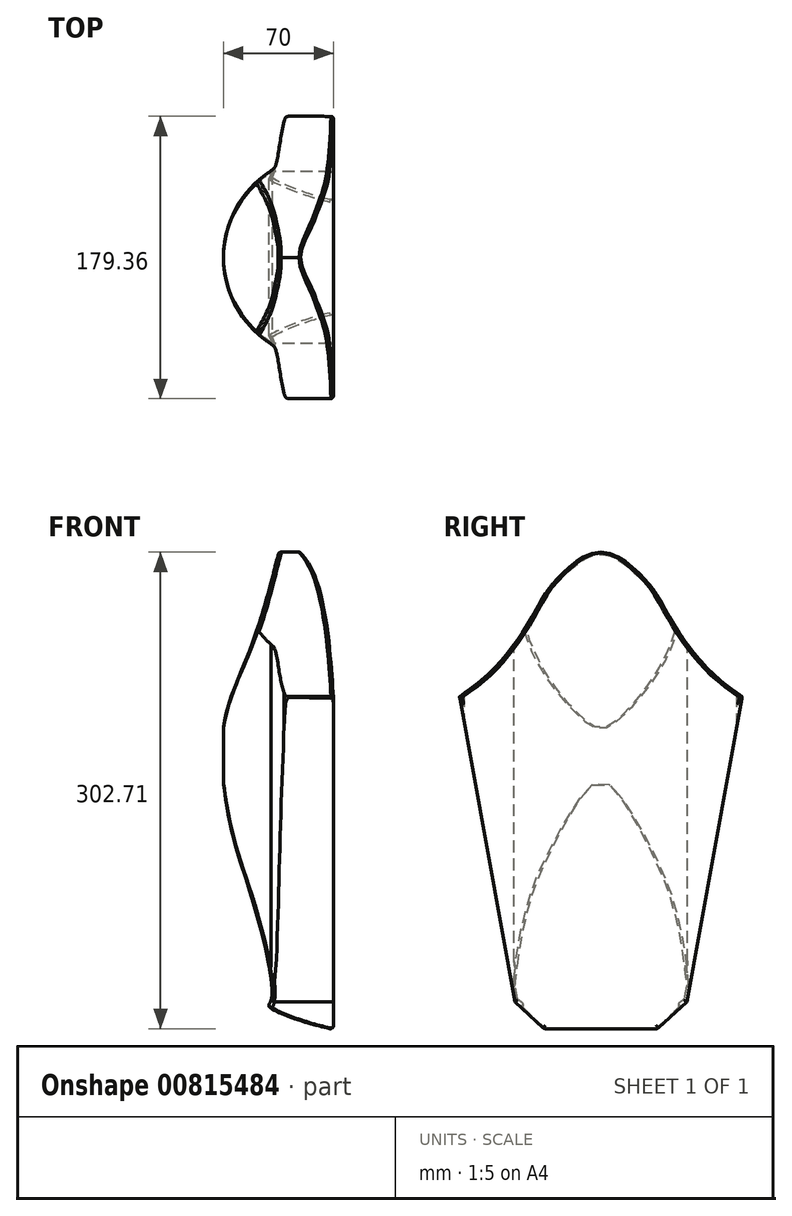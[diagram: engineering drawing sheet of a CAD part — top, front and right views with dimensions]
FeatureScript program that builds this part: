
annotation { "Feature Type Name" : "Feature", "Feature Type Description" : "" }
export const myFeature = defineFeature(function(context is Context, id is Id, definition is map)
    precondition{}
    {
        {
            var Q0;
            Q0=qCreatedBy(makeId("Right.planeOp"),FACE);
            var sketch = newSketch(context, id + "F0", { "sketchPlane" : qUnion([Q0])});
            skFitSpline(sketch, "E0", {"points": [v(0, 116.17) * mm, v(3.06, 115.78) * mm, v(7.67, 113.9) * mm, v(14.22, 108.94) * mm, v(22.25, 100.28) * mm, v(32.3, 83.46) * mm, v(42.34, 70.02) * mm, v(50.07, 62.3) * mm, v(59.84, 54.97) * mm], "startDerivative": vector(42.97, -3.15) * mm, "endDerivative": vector(75.08, -53.22) * mm});
            skLineSegment(sketch, "E1", {"start": v(59.84, 54.97) * mm, "end": v(36.42, -74.25) * mm});
            skLineSegment(sketch, "E2", {"start": v(36.42, -74.25) * mm, "end": v(17.78, -91.38) * mm});
            skLineSegment(sketch, "E3", {"start": v(17.78, -91.38) * mm, "end": v(0, -91.38) * mm});
            skLineSegment(sketch, "E4.MirrorCS", {"start": v(-59.84, 54.97) * mm, "end": v(-36.42, -74.25) * mm});
            skLineSegment(sketch, "E5.MirrorCS", {"start": v(-36.42, -74.25) * mm, "end": v(-17.78, -91.38) * mm});
            skLineSegment(sketch, "E6.MirrorCS", {"start": v(-17.78, -91.38) * mm, "end": v(0, -91.38) * mm});
            skFitSpline(sketch, "E7.MirrorCS", {"points": [v(0, 116.17) * mm, v(-3.06, 115.78) * mm, v(-7.67, 113.9) * mm, v(-14.22, 108.94) * mm, v(-22.25, 100.28) * mm, v(-32.3, 83.46) * mm, v(-42.34, 70.02) * mm, v(-50.07, 62.3) * mm, v(-59.84, 54.97) * mm], "startDerivative": vector(-42.97, -3.15) * mm, "endDerivative": vector(-75.08, -53.22) * mm});
            skSolve(sketch);
        }
        {
            var Q0;
            Q0=makeQuery(id+"F0.imprint","IMPRINT",FACE,{"disambiguationData":[TD([[makeQuery(id+"F0.imprint","IMPRINT",EDGE,{"derivedFrom":sQuery(id+"F0.wireOp",EDGE,"E0")}),-1.0]])]});
            extrude(context, id + "F1", {"entities" : qUnion([Q0]), "depth" : 65 * mm, "offsetDistance" : 25 * mm});
        }
        {
            var Q0;
            Q0=qCreatedBy(makeId("Front.planeOp"),FACE);
            cPlane(context, id + "F2", {"entities" : qUnion([Q0]), "cplaneType" : CPlaneType.OFFSET, "offset" : 75 * mm, "width" : 150 * mm, "height" : 150 * mm});
        }
        {
            var Q0;
            Q0=qCreatedBy(id+"F2.planeOp",FACE);
            var sketch = newSketch(context, id + "F3", { "sketchPlane" : qUnion([Q0])});
            skFitSpline(sketch, "E8", {"points": [v(31.28, 115.04) * mm, v(36.57, 113.68) * mm, v(49.83, 81.9) * mm, v(54.98, -86.37) * mm, v(53.81, -89.9) * mm, v(25.77, -80.55) * mm, v(26.37, -77.52) * mm, v(19.38, -38.05) * mm, v(10.13, -7.63) * mm, v(6.21, 37.7) * mm, v(18.81, 74.67) * mm, v(29.52, 111.7) * mm, v(31.28, 115.04) * mm]});
            skSolve(sketch);
        }
        {
            var Q0;
            Q0=qCreatedBy(makeId("Top.planeOp"),FACE);
            cPlane(context, id + "F4", {"entities" : qUnion([Q0]), "cplaneType" : CPlaneType.OFFSET, "offset" : 78 * mm, "oppositeDirection" : true, "width" : 150 * mm, "height" : 150 * mm});
        }
        {
            var Q0;
            Q0=qCreatedBy(id+"F4.planeOp",FACE);
            var sketch = newSketch(context, id + "F5", { "sketchPlane" : qUnion([Q0])});
            skCircle(sketch, "E9", {"center": v(36.86, 0) * mm, "radius": 3 * mm});
            skSolve(sketch);
        }
        {
            var Q0;
            Q0=qSketchRegion(id+"F5",true);
            extrude(context, id + "F6", {"entities" : qUnion([Q0]), "oppositeDirection" : true, "depth" : 27 * mm, "offsetDistance" : 25 * mm});
        }
        {
            var Q0;
            Q0=makeQuery(id+"F6.opExtrude","CAP_FACE",FACE,{"disambiguationData":[OSD([sQuery(id+"F5.wireOp",EDGE,"E9")])],"isStart":false});
            var sketch = newSketch(context, id + "F7", { "sketchPlane" : qUnion([Q0])});
            skArc(sketch, "E10", {"start": v(62.62, 0) * mm, "mid": v(49.74, 2.48) * mm, "end": v(36.86, 0) * mm});
            skArc(sketch, "E11.1.0", {"start": v(36.86, 25.76) * mm, "mid": v(34.38, 12.88) * mm, "end": v(36.86, 0) * mm});
            skArc(sketch, "E11.2.0", {"start": v(11.1, 0) * mm, "mid": v(23.98, -2.48) * mm, "end": v(36.86, 0) * mm});
            skArc(sketch, "E11.3.0", {"start": v(36.86, -25.76) * mm, "mid": v(39.34, -12.88) * mm, "end": v(36.86, 0) * mm});
            skPoint(sketch, "E11.center", {"position": v(36.86, 0) * mm});
            skFitSpline(sketch, "E12", {"points": [v(36.86, 0) * mm, v(39.57, -1.3) * mm, v(44.7, -3.53) * mm, v(53.39, -5.33) * mm, v(58.91, -4.2) * mm, v(62.07, -3.08) * mm, v(66.01, -2.63) * mm, v(62.62, 0) * mm], "startDerivative": vector(22.54, -10.77) * mm, "endDerivative": vector(-40.71, 24.26) * mm});
            skFitSpline(sketch, "E13", {"points": [v(36.86, 0) * mm, v(35.56, -2.7) * mm, v(33.33, -7.85) * mm, v(31.53, -16.53) * mm, v(32.66, -22.05) * mm, v(33.78, -25.2) * mm, v(34.23, -29.15) * mm, v(36.86, -25.76) * mm], "startDerivative": vector(-10.77, -22.54) * mm, "endDerivative": vector(24.26, 40.71) * mm});
            skFitSpline(sketch, "E14", {"points": [v(36.86, 0) * mm, v(38.16, 2.7) * mm, v(40.39, 7.85) * mm, v(42.2, 16.53) * mm, v(41.07, 22.05) * mm, v(39.94, 25.2) * mm, v(39.49, 29.15) * mm, v(36.86, 25.76) * mm], "startDerivative": vector(10.77, 22.54) * mm, "endDerivative": vector(-24.26, -40.71) * mm});
            skFitSpline(sketch, "E15", {"points": [v(36.86, 0) * mm, v(34.16, 1.3) * mm, v(29.01, 3.53) * mm, v(20.33, 5.33) * mm, v(14.81, 4.2) * mm, v(11.65, 3.08) * mm, v(7.7, 2.63) * mm, v(11.1, 0) * mm], "startDerivative": vector(-22.54, 10.77) * mm, "endDerivative": vector(40.71, -24.26) * mm});
            skSolve(sketch);
        }
        {
            var Q0;
            {var subQ0=sQuery(id+"F7.wireOp",EDGE,"E12");var subQ1=sQuery(id+"F7.wireOp",EDGE,"E10");var subQ2=makeQuery(id+"F7.imprint","INTERSECT",VERTEX,{"derivedFrom":[subQ1,subQ0]});Q0=makeQuery(id+"F7.imprint","IMPRINT",FACE,{"disambiguationData":[TD([[makeQuery(id+"F7.imprint","IMPRINT",EDGE,{"disambiguationData":[TD([[subQ2,-1.0]])],"derivedFrom":subQ1}),1.0]])]});}
            var Q1;
            {var subQ0=sQuery(id+"F7.wireOp",EDGE,"E15");var subQ1=sQuery(id+"F7.wireOp",EDGE,"E11.2.0");var subQ2=makeQuery(id+"F7.imprint","INTERSECT",VERTEX,{"derivedFrom":[subQ1,subQ0]});Q1=makeQuery(id+"F7.imprint","IMPRINT",FACE,{"disambiguationData":[TD([[makeQuery(id+"F7.imprint","IMPRINT",EDGE,{"disambiguationData":[TD([[subQ2,-1.0]])],"derivedFrom":subQ1}),1.0]])]});}
            var Q2;
            {var subQ0=sQuery(id+"F7.wireOp",EDGE,"E13");var subQ1=sQuery(id+"F7.wireOp",EDGE,"E11.3.0");var subQ2=makeQuery(id+"F7.imprint","INTERSECT",VERTEX,{"derivedFrom":[subQ1,subQ0]});Q2=makeQuery(id+"F7.imprint","IMPRINT",FACE,{"disambiguationData":[TD([[makeQuery(id+"F7.imprint","IMPRINT",EDGE,{"disambiguationData":[TD([[subQ2,-1.0]])],"derivedFrom":subQ1}),1.0]])]});}
            var Q3;
            {var subQ1=sQuery(id+"F7.wireOp",EDGE,"E11.2.0");var subQ3=makeQuery(id+"F6.opExtrude","CAP_EDGE",EDGE,{"disambiguationData":[OSD([sQuery(id+"F5.wireOp",EDGE,"E9")])],"isStart":false});var subQ4=makeQuery(id+"F7.imprint","INTERSECT",VERTEX,{"derivedFrom":[subQ3,subQ1]});Q3=makeQuery(id+"F7.imprint","IMPRINT",FACE,{"disambiguationData":[TD([[makeQuery(id+"F7.imprint","IMPRINT",EDGE,{"disambiguationData":[TD([[subQ4,-1.0]])],"derivedFrom":subQ3}),-1.0]])]});}
            var Q4;
            {var subQ0=sQuery(id+"F7.wireOp",EDGE,"E14");var subQ1=sQuery(id+"F7.wireOp",EDGE,"E11.1.0");var subQ2=makeQuery(id+"F7.imprint","INTERSECT",VERTEX,{"derivedFrom":[subQ1,subQ0]});Q4=makeQuery(id+"F7.imprint","IMPRINT",FACE,{"disambiguationData":[TD([[makeQuery(id+"F7.imprint","IMPRINT",EDGE,{"disambiguationData":[TD([[subQ2,-1.0]])],"derivedFrom":subQ1}),1.0]])]});}
            extrude(context, id + "F8", {"entities" : qUnion([Q0, Q1, Q2, Q3, Q4]), "operationType" : NewBodyOperationType.ADD, "depth" : 3 * mm, "offsetDistance" : 25 * mm});
        }
        {
            var Q0;
            Q0=qSketchRegion(id+"F5",true);
            extrude(context, id + "F9", {"entities" : qUnion([Q0]), "oppositeDirection" : true, "depth" : 32.7 * mm, "offsetDistance" : 25 * mm});
        }
        {
            var Q0;
            Q0=makeQuery(id+"F9.opExtrude","CAP_FACE",FACE,{"disambiguationData":[OSD([sQuery(id+"F5.wireOp",EDGE,"E9")])],"isStart":false});
            fillet(context, id + "F10", {"entities" : qUnion([Q0]), "radius" : 3 * mm, "tangentPropagation" : true, "allowEdgeOverflow" : false});
        }
        {
            var Q0;
            Q0=qCreatedBy(makeId("Right.planeOp"),FACE);
            cPlane(context, id + "F11", {"entities" : qUnion([Q0]), "cplaneType" : CPlaneType.OFFSET, "offset" : 60.1 * mm, "width" : 150 * mm, "height" : 150 * mm});
        }
        {
            var Q0;
            Q0=makeQuery(id+"F8.boolean.opBoolean","MERGE",BODY,{"derivedFrom":[makeQuery(id+"FMFUZFTSSeUlw5i_2.opBoolean","INTERSECT",BODY,{"derivedFrom":[makeQuery(id+"F1.opExtrude","SWEPT_BODY",BODY,{"disambiguationData":[OSD([sQuery(id+"F0.wireOp",EDGE,"E0"),sQuery(id+"F0.wireOp",EDGE,"E1"),sQuery(id+"F0.wireOp",EDGE,"E2"),sQuery(id+"F0.wireOp",EDGE,"E3"),sQuery(id+"F0.wireOp",EDGE,"E4.MirrorCS"),sQuery(id+"F0.wireOp",EDGE,"E5.MirrorCS"),sQuery(id+"F0.wireOp",EDGE,"E6.MirrorCS"),sQuery(id+"F0.wireOp",EDGE,"E7.MirrorCS")])]}),makeQuery(id+"FxEsF20hEnfzxVD_1.opExtrude","SWEPT_BODY",BODY,{"disambiguationData":[OSD([sQuery(id+"F3.wireOp",EDGE,"E8")])]})]}),makeQuery(id+"F8.opExtrude","SWEPT_BODY",BODY,{"disambiguationData":[OSD([sQuery(id+"F5.wireOp",EDGE,"E9"),sQuery(id+"F7.wireOp",EDGE,"E10"),sQuery(id+"F7.wireOp",EDGE,"E12")])]})]});
            var Q1;
            {var subQ0=sQuery(id+"F5.wireOp",EDGE,"E9");Q1=makeQuery(id+"F8.boolean.opBoolean","MERGE",BODY,{"derivedFrom":[makeQuery(id+"FMFUZFTSSeUlw5i_2.opBoolean","INTERSECT",BODY,{"derivedFrom":[makeQuery(id+"F1.opExtrude","SWEPT_BODY",BODY,{"disambiguationData":[OSD([sQuery(id+"F0.wireOp",EDGE,"E0"),sQuery(id+"F0.wireOp",EDGE,"E1"),sQuery(id+"F0.wireOp",EDGE,"E2"),sQuery(id+"F0.wireOp",EDGE,"E3"),sQuery(id+"F0.wireOp",EDGE,"E4.MirrorCS"),sQuery(id+"F0.wireOp",EDGE,"E5.MirrorCS"),sQuery(id+"F0.wireOp",EDGE,"E6.MirrorCS"),sQuery(id+"F0.wireOp",EDGE,"E7.MirrorCS")])]}),makeQuery(id+"FxEsF20hEnfzxVD_1.opExtrude","SWEPT_BODY",BODY,{"disambiguationData":[OSD([sQuery(id+"F3.wireOp",EDGE,"E8")])]})]}),makeQuery(id+"F8.opExtrude","SWEPT_BODY",BODY,{"disambiguationData":[OSD([subQ0,sQuery(id+"F7.wireOp",EDGE,"E10"),sQuery(id+"F7.wireOp",EDGE,"E12")])]}),makeQuery(id+"F8.opExtrude","SWEPT_BODY",BODY,{"disambiguationData":[OSD([subQ0,sQuery(id+"F7.wireOp",EDGE,"E11.1.0"),sQuery(id+"F7.wireOp",EDGE,"E14")])]})]});}
            var Q2;
            {var subQ0=sQuery(id+"F5.wireOp",EDGE,"E9");Q2=makeQuery(id+"F8.boolean.opBoolean","MERGE",BODY,{"derivedFrom":[makeQuery(id+"FMFUZFTSSeUlw5i_2.opBoolean","INTERSECT",BODY,{"derivedFrom":[makeQuery(id+"F1.opExtrude","SWEPT_BODY",BODY,{"disambiguationData":[OSD([sQuery(id+"F0.wireOp",EDGE,"E0"),sQuery(id+"F0.wireOp",EDGE,"E1"),sQuery(id+"F0.wireOp",EDGE,"E2"),sQuery(id+"F0.wireOp",EDGE,"E3"),sQuery(id+"F0.wireOp",EDGE,"E4.MirrorCS"),sQuery(id+"F0.wireOp",EDGE,"E5.MirrorCS"),sQuery(id+"F0.wireOp",EDGE,"E6.MirrorCS"),sQuery(id+"F0.wireOp",EDGE,"E7.MirrorCS")])]}),makeQuery(id+"FxEsF20hEnfzxVD_1.opExtrude","SWEPT_BODY",BODY,{"disambiguationData":[OSD([sQuery(id+"F3.wireOp",EDGE,"E8")])]})]}),makeQuery(id+"F8.opExtrude","SWEPT_BODY",BODY,{"disambiguationData":[OSD([subQ0,sQuery(id+"F7.wireOp",EDGE,"E10"),sQuery(id+"F7.wireOp",EDGE,"E12")])]}),makeQuery(id+"F8.opExtrude","SWEPT_BODY",BODY,{"disambiguationData":[OSD([subQ0,sQuery(id+"F7.wireOp",EDGE,"E11.1.0"),sQuery(id+"F7.wireOp",EDGE,"E14")])]}),makeQuery(id+"F8.opExtrude","SWEPT_BODY",BODY,{"disambiguationData":[OSD([sQuery(id+"F7.wireOp",EDGE,"E11.2.0"),sQuery(id+"F7.wireOp",EDGE,"E15")])]}),makeQuery(id+"F8.opExtrude","SWEPT_BODY",BODY,{"disambiguationData":[OSD([subQ0,sQuery(id+"F7.wireOp",EDGE,"E11.3.0"),sQuery(id+"F7.wireOp",EDGE,"E13")])]})]});}
            var Q3;
            Q3=makeQuery(id+"F9.opExtrude","SWEPT_BODY",BODY,{"disambiguationData":[OSD([sQuery(id+"F5.wireOp",EDGE,"E9")])]});
            deleteBodies(context, id + "F12", {"entities" : qUnion([Q0, Q1, Q2, Q3])});
        }
        {
            var Q0;
            Q0=makeQuery(id+"F6.opExtrude","SWEPT_BODY",BODY,{"disambiguationData":[OSD([sQuery(id+"F5.wireOp",EDGE,"E9")])]});
            deleteBodies(context, id + "F13", {"entities" : qUnion([Q0])});
        }
        {
            var Q0;
            Q0=makeQuery(id+"F1.opExtrude","SWEPT_BODY",BODY,{"disambiguationData":[OSD([sQuery(id+"F0.wireOp",EDGE,"E0"),sQuery(id+"F0.wireOp",EDGE,"E1"),sQuery(id+"F0.wireOp",EDGE,"E2"),sQuery(id+"F0.wireOp",EDGE,"E3"),sQuery(id+"F0.wireOp",EDGE,"E4.MirrorCS"),sQuery(id+"F0.wireOp",EDGE,"E5.MirrorCS"),sQuery(id+"F0.wireOp",EDGE,"E6.MirrorCS"),sQuery(id+"F0.wireOp",EDGE,"E7.MirrorCS")])]});
            var Q1;
            Q1=qCreatedBy(makeId("Origin.pointOp"),VERTEX);
            transform(context, id + "F14", {"entities" : qUnion([Q0]), "transformType" : TransformType.SCALE_UNIFORMLY, "scale" : 1.5, "scalePoint" : qUnion([Q1]), "makeCopy" : false});
        }
        {
            var Q0;
            Q0=qCreatedBy(makeId("Front.planeOp"),FACE);
            cPlane(context, id + "F15", {"entities" : qUnion([Q0]), "cplaneType" : CPlaneType.OFFSET, "offset" : 104 * mm, "width" : 150 * mm, "height" : 150 * mm});
        }
        {
            var Q0;
            Q0=qCreatedBy(id+"F15.planeOp",FACE);
            var sketch = newSketch(context, id + "F16", { "sketchPlane" : qUnion([Q0])});
            skFitSpline(sketch, "E16", {"points": [v(43.42, 119.03) * mm, v(48.72, 117.67) * mm, v(61.97, 85.89) * mm, v(67.12, -82.39) * mm, v(65.95, -85.92) * mm, v(37.91, -76.56) * mm, v(38.52, -73.54) * mm, v(31.52, -34.07) * mm, v(22.28, -3.64) * mm, v(18.36, 41.68) * mm, v(30.95, 78.65) * mm, v(41.66, 115.7) * mm, v(43.42, 119.03) * mm]});
            skSolve(sketch);
        }
        {
            var Q0;
            Q0=makeQuery(id+"F16.imprint","IMPRINT",FACE,{"disambiguationData":[TD([[makeQuery(id+"F16.imprint","IMPRINT",EDGE,{"derivedFrom":sQuery(id+"F16.wireOp",EDGE,"E16")}),-1.0]])]});
            extrude(context, id + "F17", {"entities" : qUnion([Q0]), "depth" : 25 * mm, "offsetDistance" : 25 * mm});
        }
        {
            var Q0;
            Q0=makeQuery(id+"F17.opExtrude","SWEPT_BODY",BODY,{"disambiguationData":[OSD([sQuery(id+"F16.wireOp",EDGE,"E16")])]});
            var Q1;
            Q1=qCreatedBy(makeId("Origin.pointOp"),VERTEX);
            transform(context, id + "F18", {"entities" : qUnion([Q0]), "transformType" : TransformType.SCALE_UNIFORMLY, "scale" : 1.5, "scalePoint" : qUnion([Q1]), "makeCopy" : false});
        }
        {
            var Q0;
            Q0=qCreatedBy(makeId("Top.planeOp"),FACE);
            cPlane(context, id + "F19", {"entities" : qUnion([Q0]), "cplaneType" : CPlaneType.OFFSET, "offset" : 208 * mm, "width" : 150 * mm, "height" : 150 * mm});
        }
        {
            var Q0;
            Q0=qCreatedBy(id+"F19.planeOp",FACE);
            var sketch = newSketch(context, id + "F20", { "sketchPlane" : qUnion([Q0])});
            skArc(sketch, "E17", {"start": v(57.86, 55) * mm, "mid": v(27.5, 0) * mm, "end": v(57.86, -55) * mm});
            skFitSpline(sketch, "E18", {"points": [v(57.86, -55) * mm, v(60.33, -57.67) * mm, v(61.34, -60.55) * mm, v(62.35, -66.03) * mm, v(64.22, -77.55) * mm, v(66.1, -86.48) * mm], "startDerivative": vector(25.4, -23.73) * mm, "endDerivative": vector(8.71, -36.77) * mm});
            skFitSpline(sketch, "E19.MirrorCS", {"points": [v(66.1, -86.48) * mm, v(67, -88.97) * mm, v(67.52, -89.33) * mm, v(68.83, -89.68) * mm], "startDerivative": vector(2, -6.79) * mm, "endDerivative": vector(4.54, -1.13) * mm});
            skLineSegment(sketch, "E20", {"start": v(27, -156) * mm, "end": v(27, 124.27) * mm, "construction": true});
            skFitSpline(sketch, "E21", {"points": [v(57.86, -55) * mm, v(57.86, -55) * mm], "startDerivative": vector(0, 0) * mm, "endDerivative": vector(0, 0) * mm});
            skFitSpline(sketch, "E22.MirrorCS", {"points": [v(57.86, 55) * mm, v(60.33, 57.67) * mm, v(61.34, 60.55) * mm, v(62.35, 66.03) * mm, v(64.22, 77.55) * mm, v(66.1, 86.48) * mm], "startDerivative": vector(25.4, 23.73) * mm, "endDerivative": vector(8.71, 36.77) * mm});
            skFitSpline(sketch, "E23.MirrorCS", {"points": [v(66.1, 86.48) * mm, v(67, 88.97) * mm, v(67.52, 89.33) * mm, v(68.83, 89.68) * mm], "startDerivative": vector(2, 6.79) * mm, "endDerivative": vector(4.54, 1.13) * mm});
            skFitSpline(sketch, "E24", {"points": [v(57.86, 55) * mm, v(57.86, 55) * mm], "startDerivative": vector(0, 0) * mm, "endDerivative": vector(0, 0) * mm});
            skLineSegment(sketch, "E25", {"start": v(68.83, -89.68) * mm, "end": v(97.5, -89.56) * mm});
            skLineSegment(sketch, "E26.MirrorCS", {"start": v(68.83, 89.68) * mm, "end": v(97.5, 89.56) * mm});
            skLineSegment(sketch, "E27", {"start": v(97.5, 89.56) * mm, "end": v(97.5, -89.56) * mm});
            skSolve(sketch);
        }
        {
            var Q0;
            Q0=makeQuery(id+"F20.imprint","IMPRINT",FACE,{"disambiguationData":[TD([[makeQuery(id+"F20.imprint","IMPRINT",EDGE,{"derivedFrom":sQuery(id+"F20.wireOp",EDGE,"E17")}),1.0]])]});
            extrude(context, id + "F21", {"entities" : qUnion([Q0]), "oppositeDirection" : true, "depth" : 416 * mm, "offsetDistance" : 25 * mm});
        }
        {
            var Q0;
            Q0=makeQuery(id+"F17.opExtrude","CAP_FACE",FACE,{"disambiguationData":[OSD([sQuery(id+"F16.wireOp",EDGE,"E16")])],"isStart":true});
            extrude(context, id + "F22", {"entities" : qUnion([Q0]), "depth" : 259 * mm, "offsetDistance" : 25 * mm});
        }
        {
            var Q0;
            Q0=makeQuery(id+"F1.opExtrude","SWEPT_BODY",BODY,{"disambiguationData":[OSD([sQuery(id+"F0.wireOp",EDGE,"E0"),sQuery(id+"F0.wireOp",EDGE,"E1"),sQuery(id+"F0.wireOp",EDGE,"E2"),sQuery(id+"F0.wireOp",EDGE,"E3"),sQuery(id+"F0.wireOp",EDGE,"E4.MirrorCS"),sQuery(id+"F0.wireOp",EDGE,"E5.MirrorCS"),sQuery(id+"F0.wireOp",EDGE,"E6.MirrorCS"),sQuery(id+"F0.wireOp",EDGE,"E7.MirrorCS")])]});
            var Q1;
            Q1=makeQuery(id+"F21.opExtrude","SWEPT_BODY",BODY,{"disambiguationData":[OSD([sQuery(id+"F20.wireOp",EDGE,"E17"),sQuery(id+"F20.wireOp",EDGE,"E18"),sQuery(id+"F20.wireOp",EDGE,"E19.MirrorCS"),sQuery(id+"F20.wireOp",EDGE,"E21"),sQuery(id+"F20.wireOp",EDGE,"E22.MirrorCS"),sQuery(id+"F20.wireOp",EDGE,"E23.MirrorCS"),sQuery(id+"F20.wireOp",EDGE,"E24"),sQuery(id+"F20.wireOp",EDGE,"E25"),sQuery(id+"F20.wireOp",EDGE,"E26.MirrorCS"),sQuery(id+"F20.wireOp",EDGE,"E27")])]});
            var Q2;
            Q2=makeQuery(id+"F22.opExtrude","SWEPT_BODY",BODY,{"disambiguationData":[OSD([sQuery(id+"F16.wireOp",EDGE,"E16")])]});
            booleanBodies(context, id + "F23", {"operationType" : BooleanOperationType.INTERSECTION, "tools" : qUnion([Q0, Q1, Q2])});
        }
        {
            var Q0;
            Q0=makeQuery(id+"F17.opExtrude","SWEPT_BODY",BODY,{"disambiguationData":[OSD([sQuery(id+"F16.wireOp",EDGE,"E16")])]});
            deleteBodies(context, id + "F24", {"entities" : qUnion([Q0])});
        }
        {
            var Q0;
            {var subQ0=sQuery(id+"F0.wireOp",EDGE,"E4.MirrorCS");var subQ1=sQuery(id+"F0.wireOp",EDGE,"E2");var subQ2=sQuery(id+"F0.wireOp",EDGE,"E1");var subQ3=sQuery(id+"F0.wireOp",EDGE,"E5.MirrorCS");Q0=makeQuery(id+"F23.opBoolean","SPLIT",FACE,{"disambiguationData":[TD([makeQuery(id+"F1.opExtrude","CAP_FACE",FACE,{"disambiguationData":[OSD([sQuery(id+"F0.wireOp",EDGE,"E0"),subQ2,subQ1,sQuery(id+"F0.wireOp",EDGE,"E3"),subQ0,subQ3,sQuery(id+"F0.wireOp",EDGE,"E6.MirrorCS"),sQuery(id+"F0.wireOp",EDGE,"E7.MirrorCS")])],"isStart":false}),makeQuery(id+"F1.opExtrude","SWEPT_FACE",FACE,{"disambiguationData":[OSD([subQ2])]}),makeQuery(id+"F1.opExtrude","SWEPT_FACE",FACE,{"disambiguationData":[OSD([subQ1])]}),makeQuery(id+"F1.opExtrude","SWEPT_FACE",FACE,{"disambiguationData":[OSD([subQ0])]}),makeQuery(id+"F1.opExtrude","SWEPT_FACE",FACE,{"disambiguationData":[OSD([subQ3])]}),makeQuery(id+"F21.opExtrude","SWEPT_FACE",FACE,{"disambiguationData":[OSD([sQuery(id+"F20.wireOp",EDGE,"E17")])]}),makeQuery(id+"F21.opExtrude","SWEPT_FACE",FACE,{"disambiguationData":[OSD([sQuery(id+"F20.wireOp",EDGE,"E18")])]}),makeQuery(id+"F21.opExtrude","SWEPT_FACE",FACE,{"disambiguationData":[OSD([sQuery(id+"F20.wireOp",EDGE,"E21")])]}),makeQuery(id+"F21.opExtrude","SWEPT_FACE",FACE,{"disambiguationData":[OSD([sQuery(id+"F20.wireOp",EDGE,"E22.MirrorCS")])]}),makeQuery(id+"F21.opExtrude","SWEPT_FACE",FACE,{"disambiguationData":[OSD([sQuery(id+"F20.wireOp",EDGE,"E24")])]})])],"derivedFrom":makeQuery(id+"F22.opExtrude","SWEPT_FACE",FACE,{"disambiguationData":[OSD([sQuery(id+"F16.wireOp",EDGE,"E16")])]})});}
            var Q1;
            Q1=makeQuery(id+"F23.opBoolean","SPLIT",FACE,{"disambiguationData":[TD([makeQuery(id+"F1.opExtrude","SWEPT_FACE",FACE,{"disambiguationData":[OSD([sQuery(id+"F0.wireOp",EDGE,"E0")])]}),makeQuery(id+"F1.opExtrude","SWEPT_FACE",FACE,{"disambiguationData":[OSD([sQuery(id+"F0.wireOp",EDGE,"E7.MirrorCS")])]}),makeQuery(id+"F21.opExtrude","SWEPT_FACE",FACE,{"disambiguationData":[OSD([sQuery(id+"F20.wireOp",EDGE,"E17")])]})])],"derivedFrom":makeQuery(id+"F22.opExtrude","SWEPT_FACE",FACE,{"disambiguationData":[OSD([sQuery(id+"F16.wireOp",EDGE,"E16")])]})});
            fillet(context, id + "F25", {"entities" : qUnion([Q0, Q1]), "radius" : 2 * mm, "tangentPropagation" : true, "allowEdgeOverflow" : false});
        }
        {
            var Q0;
            Q0=makeQuery(id+"F1.opExtrude","CAP_FACE",FACE,{"disambiguationData":[OSD([sQuery(id+"F0.wireOp",EDGE,"E0"),sQuery(id+"F0.wireOp",EDGE,"E1"),sQuery(id+"F0.wireOp",EDGE,"E2"),sQuery(id+"F0.wireOp",EDGE,"E3"),sQuery(id+"F0.wireOp",EDGE,"E4.MirrorCS"),sQuery(id+"F0.wireOp",EDGE,"E5.MirrorCS"),sQuery(id+"F0.wireOp",EDGE,"E6.MirrorCS"),sQuery(id+"F0.wireOp",EDGE,"E7.MirrorCS")])],"isStart":false});
            fillet(context, id + "F26", {"entities" : qUnion([Q0]), "radius" : 2 * mm, "tangentPropagation" : true, "allowEdgeOverflow" : false});
        }
        {
            var Q0;
            {var subQ0=sQuery(id+"F0.wireOp",EDGE,"E4.MirrorCS");var subQ1=sQuery(id+"F0.wireOp",EDGE,"E1");var subQ2=sQuery(id+"F0.wireOp",EDGE,"E7.MirrorCS");var subQ3=sQuery(id+"F0.wireOp",EDGE,"E0");Q0=makeQuery(id+"F23.opBoolean","SPLIT",FACE,{"disambiguationData":[TD([makeQuery(id+"F1.opExtrude","SWEPT_FACE",FACE,{"disambiguationData":[OSD([subQ3])]}),makeQuery(id+"F1.opExtrude","CAP_FACE",FACE,{"disambiguationData":[OSD([subQ3,subQ1,sQuery(id+"F0.wireOp",EDGE,"E2"),sQuery(id+"F0.wireOp",EDGE,"E3"),subQ0,sQuery(id+"F0.wireOp",EDGE,"E5.MirrorCS"),sQuery(id+"F0.wireOp",EDGE,"E6.MirrorCS"),subQ2])],"isStart":false}),makeQuery(id+"F1.opExtrude","SWEPT_FACE",FACE,{"disambiguationData":[OSD([subQ1])]}),makeQuery(id+"F1.opExtrude","SWEPT_FACE",FACE,{"disambiguationData":[OSD([subQ0])]}),makeQuery(id+"F1.opExtrude","SWEPT_FACE",FACE,{"disambiguationData":[OSD([subQ2])]}),makeQuery(id+"F21.opExtrude","SWEPT_FACE",FACE,{"disambiguationData":[OSD([sQuery(id+"F20.wireOp",EDGE,"E25")])]}),makeQuery(id+"F21.opExtrude","SWEPT_FACE",FACE,{"disambiguationData":[OSD([sQuery(id+"F20.wireOp",EDGE,"E26.MirrorCS")])]})])],"derivedFrom":makeQuery(id+"F22.opExtrude","SWEPT_FACE",FACE,{"disambiguationData":[OSD([sQuery(id+"F16.wireOp",EDGE,"E16")])]})});}
            fillet(context, id + "F27", {"entities" : qUnion([Q0]), "radius" : 1.5 * mm, "tangentPropagation" : true, "allowEdgeOverflow" : false});
        }
    });
